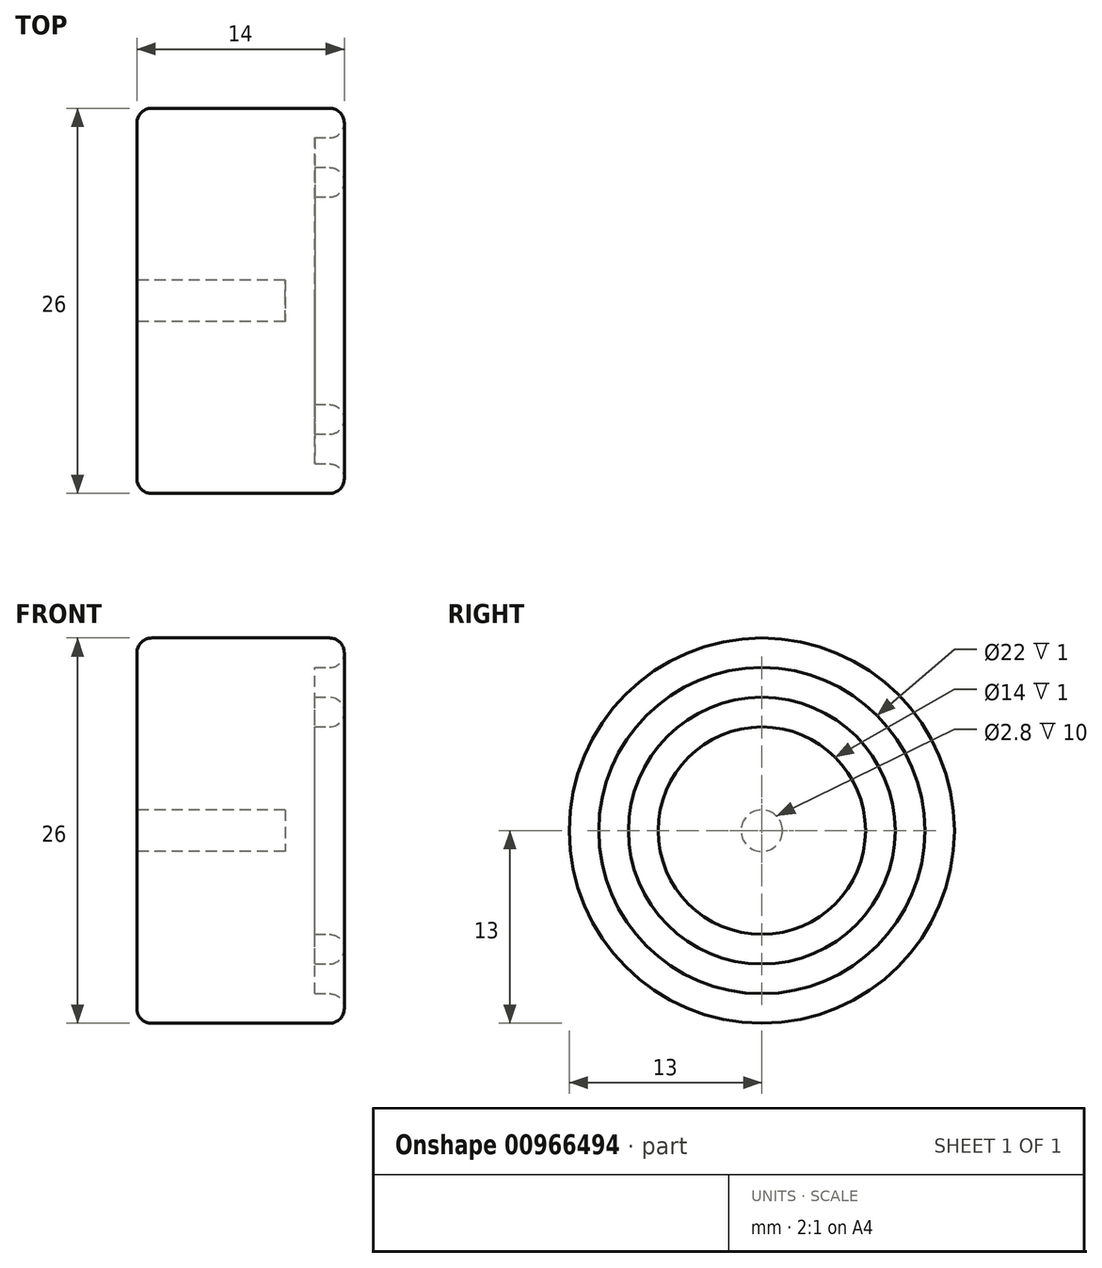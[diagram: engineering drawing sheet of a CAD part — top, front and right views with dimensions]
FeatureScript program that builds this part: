
annotation { "Feature Type Name" : "Feature", "Feature Type Description" : "" }
export const myFeature = defineFeature(function(context is Context, id is Id, definition is map)
    precondition{}
    {
        {
            var Q0;
            Q0=qCreatedBy(makeId("Front.planeOp"),FACE);
            var sketch = newSketch(context, id + "F0", { "sketchPlane" : qUnion([Q0])});
            skLineSegment(sketch, "E0.bottom", {"start": v(0, 0) * mm, "end": v(-12, 0) * mm});
            skLineSegment(sketch, "E0.top", {"start": v(0, 13) * mm, "end": v(-12, 13) * mm});
            skLineSegment(sketch, "E0.left", {"start": v(0, 0) * mm, "end": v(0, 13) * mm});
            skLineSegment(sketch, "E0.right", {"start": v(-12, 0) * mm, "end": v(-12, 13) * mm});
            skLineSegment(sketch, "E1.bottom", {"start": v(2, 13) * mm, "end": v(-12, 13) * mm});
            skLineSegment(sketch, "E1.top", {"start": v(2, 11) * mm, "end": v(-12, 11) * mm});
            skLineSegment(sketch, "E1.left", {"start": v(2, 13) * mm, "end": v(2, 11) * mm});
            skLineSegment(sketch, "E2", {"start": v(4.7, 11) * mm, "end": v(4.7, 12.75) * mm, "construction": true});
            skLineSegment(sketch, "E3", {"start": v(8.15, 11) * mm, "end": v(8.15, 9) * mm, "construction": true});
            skLineSegment(sketch, "E4.bottom", {"start": v(0, 9) * mm, "end": v(2, 9) * mm});
            skLineSegment(sketch, "E4.top", {"start": v(0, 7) * mm, "end": v(2, 7) * mm});
            skLineSegment(sketch, "E4.left", {"start": v(0, 9) * mm, "end": v(0, 7) * mm});
            skLineSegment(sketch, "E4.right", {"start": v(2, 9) * mm, "end": v(2, 7) * mm});
            skPoint(sketch, "E5.orphan", {"position": v(-14, 13) * mm});
            skSolve(sketch);
        }
        {
            var Q0;
            Q0=qSketchRegion(id+"F0",true);
            var Q1;
            Q1=sQuery(id+"F0.wireOp",EDGE,"E0.bottom");
            revolve(context, id + "F1", {"surfaceOperationType" : NewSurfaceOperationType.NEW, "entities" : qUnion([Q0]), "axis" : qUnion([Q1]), "revolveType" : RevolveType.FULL});
        }
        {
            var Q0;
            Q0=makeQuery(id+"F1.opRevolve","SWEPT_EDGE",EDGE,{"disambiguationData":[OSD([sQuery(id+"F0.wireOp",EDGE,"E1.bottom"),sQuery(id+"F0.wireOp",EDGE,"E1.left")])]});
            var Q1;
            Q1=makeQuery(id+"F1.opRevolve","SWEPT_EDGE",EDGE,{"disambiguationData":[OSD([sQuery(id+"F0.wireOp",EDGE,"E4.bottom"),sQuery(id+"F0.wireOp",EDGE,"E4.right")])]});
            var Q2;
            Q2=makeQuery(id+"F1.opRevolve","SWEPT_EDGE",EDGE,{"disambiguationData":[OSD([sQuery(id+"F0.wireOp",EDGE,"E4.top"),sQuery(id+"F0.wireOp",EDGE,"E4.right")])]});
            var Q3;
            Q3=makeQuery(id+"F1.opRevolve","SWEPT_EDGE",EDGE,{"disambiguationData":[OSD([sQuery(id+"F0.wireOp",EDGE,"E1.top"),sQuery(id+"F0.wireOp",EDGE,"E1.left")])]});
            var Q4;
            Q4=makeQuery(id+"F1.opRevolve","SWEPT_EDGE",EDGE,{"disambiguationData":[OSD([sQuery(id+"F0.wireOp",EDGE,"E0.right"),sQuery(id+"F0.wireOp",EDGE,"E1.bottom")])]});
            fillet(context, id + "F2", {"entities" : qUnion([Q0, Q1, Q2, Q3, Q4]), "radius" : 1 * mm, "tangentPropagation" : true, "allowEdgeOverflow" : false});
        }
        {
            var Q0;
            Q0=makeQuery(id+"F1.opRevolve","SWEPT_FACE",FACE,{"disambiguationData":[OSD([sQuery(id+"F0.wireOp",EDGE,"E0.right")])]});
            var sketch = newSketch(context, id + "F3", { "sketchPlane" : qUnion([Q0])});
            skCircle(sketch, "E6", {"center": v(0, 0) * mm, "radius": 1.4 * mm});
            skSolve(sketch);
        }
        {
            var Q0;
            Q0=makeQuery(id+"F3.imprint","IMPRINT",FACE,{"disambiguationData":[TD([[makeQuery(id+"F3.imprint","IMPRINT",EDGE,{"derivedFrom":sQuery(id+"F3.wireOp",EDGE,"E6")}),1.0]])]});
            extrude(context, id + "F4", {"entities" : qUnion([Q0]), "operationType" : NewBodyOperationType.REMOVE, "oppositeDirection" : true, "depth" : 10 * mm, "offsetDistance" : 25 * mm});
        }
    });
